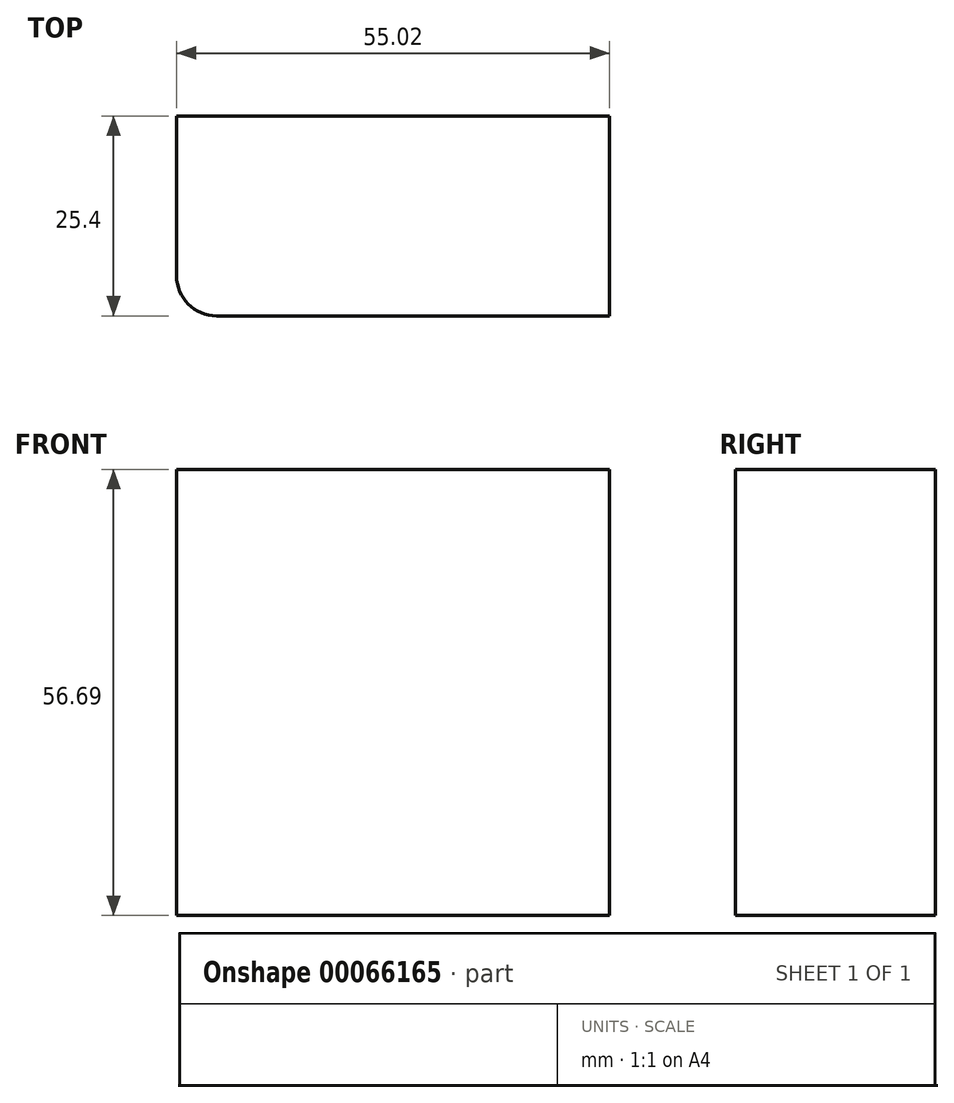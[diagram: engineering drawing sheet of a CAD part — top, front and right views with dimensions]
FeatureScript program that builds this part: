
annotation { "Feature Type Name" : "Feature", "Feature Type Description" : "" }
export const myFeature = defineFeature(function(context is Context, id is Id, definition is map)
    precondition{}
    {
        {
            var Q0;
            Q0=qCreatedBy(makeId("Front.planeOp"),FACE);
            var sketch = newSketch(context, id + "F0", { "sketchPlane" : qUnion([Q0])});
            skLineSegment(sketch, "E0.bottom", {"start": v(-27.03, 29.78) * mm, "end": v(27.99, 29.78) * mm});
            skLineSegment(sketch, "E0.top", {"start": v(-27.03, -26.9) * mm, "end": v(27.99, -26.9) * mm});
            skLineSegment(sketch, "E0.left", {"start": v(-27.03, 29.78) * mm, "end": v(-27.03, -26.9) * mm});
            skLineSegment(sketch, "E0.right", {"start": v(27.99, 29.78) * mm, "end": v(27.99, -26.9) * mm});
            skSolve(sketch);
        }
        {
            var Q0;
            Q0 = qSketchRegion(id + "F0", true);
            extrude(context, id + "F1", {"entities" : qUnion([Q0]), "depth" : 25.4 * mm});
        }
        {
            var Q0;
            Q0=makeQuery(id+"F1.opExtrude","CAP_EDGE",EDGE,{"disambiguationData":[OSD([sQuery(id+"F0.wireOp",EDGE,"E0.left")])],"isStart":false});
            fillet(context, id + "F2", {"entities" : qUnion([Q0]), "radius" : 5.08 * mm, "tangentPropagation" : true, "allowEdgeOverflow" : false});
        }
    });
